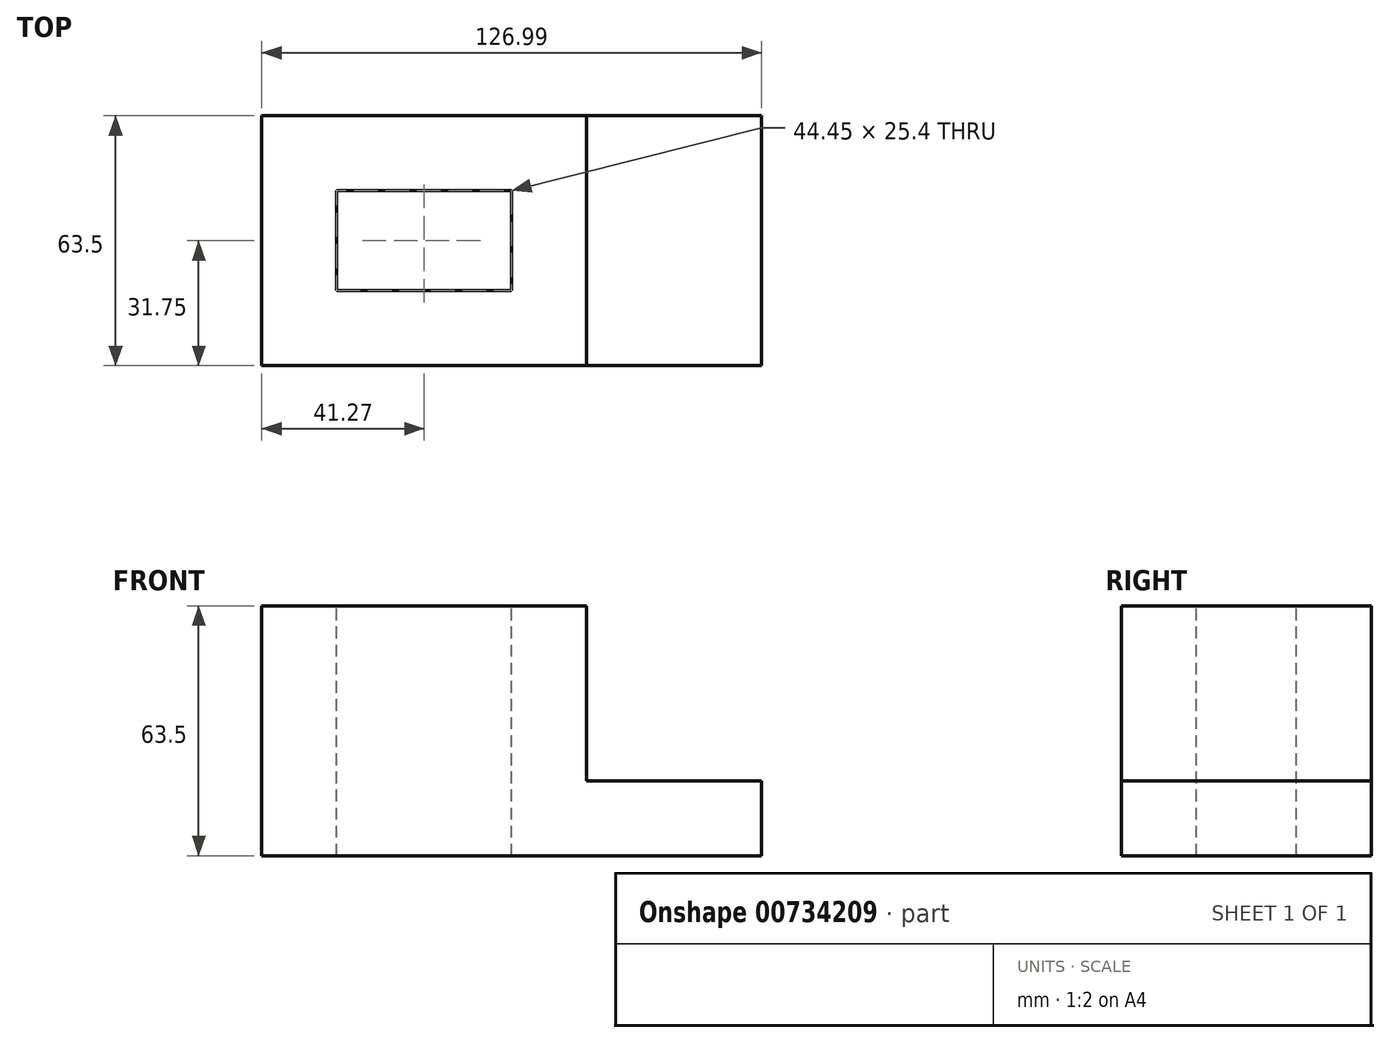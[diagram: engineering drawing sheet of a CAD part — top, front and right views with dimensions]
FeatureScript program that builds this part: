
annotation { "Feature Type Name" : "Feature", "Feature Type Description" : "" }
export const myFeature = defineFeature(function(context is Context, id is Id, definition is map)
    precondition{}
    {
        {
            var Q0;
            Q0=qCreatedBy(makeId("Front.planeOp"),FACE);
            var sketch = newSketch(context, id + "F0", { "sketchPlane" : qUnion([Q0])});
            skLineSegment(sketch, "E0.bottom", {"start": v(-41.28, -31.75) * mm, "end": v(41.27, -31.75) * mm});
            skLineSegment(sketch, "E0.top", {"start": v(-41.28, 31.75) * mm, "end": v(41.28, 31.75) * mm});
            skLineSegment(sketch, "E0.left", {"start": v(-41.28, -31.75) * mm, "end": v(-41.28, 31.75) * mm});
            skPoint(sketch, "E0.middle", {"position": v(0, 0) * mm});
            skLineSegment(sketch, "E1.bottom", {"start": v(41.28, -31.75) * mm, "end": v(85.73, -31.75) * mm});
            skLineSegment(sketch, "E1.top", {"start": v(41.28, -12.7) * mm, "end": v(85.73, -12.7) * mm});
            skLineSegment(sketch, "E1.right", {"start": v(85.73, -31.75) * mm, "end": v(85.73, -12.7) * mm});
            skLineSegment(sketch, "E2", {"start": v(41.28, 31.75) * mm, "end": v(41.28, -12.7) * mm});
            skSolve(sketch);
        }
        {
            var Q0;
            Q0=makeQuery(id+"F0.imprint","IMPRINT",FACE,{"disambiguationData":[TD([[makeQuery(id+"F0.imprint","IMPRINT",EDGE,{"derivedFrom":sQuery(id+"F0.wireOp",EDGE,"E0.bottom")}),1.0]])]});
            extrude(context, id + "F1", {"entities" : qUnion([Q0]), "depth" : 63.5 * mm, "offsetDistance" : 25.4 * mm});
        }
        {
            var Q0;
            Q0=makeQuery(id+"F1.opExtrude","SWEPT_FACE",FACE,{"disambiguationData":[OSD([sQuery(id+"F0.wireOp",EDGE,"E0.top")])]});
            var sketch = newSketch(context, id + "F2", { "sketchPlane" : qUnion([Q0])});
            skLineSegment(sketch, "E3.bottom", {"start": v(-22.23, -19.05) * mm, "end": v(22.23, -19.05) * mm});
            skLineSegment(sketch, "E3.top", {"start": v(-22.23, -44.45) * mm, "end": v(22.23, -44.45) * mm});
            skLineSegment(sketch, "E3.left", {"start": v(-22.23, -19.05) * mm, "end": v(-22.23, -44.45) * mm});
            skLineSegment(sketch, "E3.right", {"start": v(22.23, -19.05) * mm, "end": v(22.23, -44.45) * mm});
            skSolve(sketch);
        }
        {
            var Q0;
            Q0=makeQuery(id+"F2.imprint","IMPRINT",FACE,{"disambiguationData":[TD([[makeQuery(id+"F2.imprint","IMPRINT",EDGE,{"derivedFrom":sQuery(id+"F2.wireOp",EDGE,"E3.bottom")}),-1.0]])]});
            extrude(context, id + "F3", {"entities" : qUnion([Q0]), "operationType" : NewBodyOperationType.REMOVE, "oppositeDirection" : true, "depth" : 63.5 * mm, "offsetDistance" : 25.4 * mm});
        }
    });
